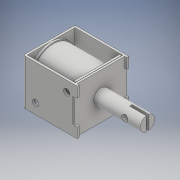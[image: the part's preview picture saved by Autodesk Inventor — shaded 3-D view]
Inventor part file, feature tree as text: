
AUTODESK INVENTOR PART (.ipt)
format: ipt  version: 2017 (Build 210142000, 142)  size: 295,936 bytes
history: native  units: mm
features: extrude x14, sketch x14, other x5, mirror x4, fillet x3
ambient origin geometry x8: Origin, YZ Plane, XZ Plane, XY Plane, X Axis, Y Axis, Z Axis, Center Point
bodies: Body1 (feature_tree)
feature tree (40):
  other  "Твердое тело1"
  extrude  "Выдавливание1"  Depth=25.0mm
  extrude  "Выдавливание4"  Depth=26.0mm
  extrude  "Выдавливание5"  Depth=22.0mm TaperAngle=0.0deg
  extrude  "Выдавливание6"  Depth=1.0mm
  extrude  "Выдавливание7"  Depth=1.0mm
  extrude  "Выдавливание8"  Depth=1.0mm
  other  "РабПлоскость1"
  extrude  "Выдавливание11"  Depth=25.0mm TaperAngle=0.0deg
  other  "РабПлоскость2"
  extrude  "Выдавливание12"  Depth=5.0mm
  extrude  "Выдавливание13"  Depth=5.0mm
  mirror  "Зеркальное отражение1"
  mirror  "Зеркальное отражение2"
  extrude  "Выдавливание14"  Depth=2.0mm
  other  "РабПлоскость3"
  extrude  "Выдавливание15"  Depth=25.0mm TaperAngle=0.0deg
  mirror  "Зеркальное отражение3"
  fillet  "Сопряжение1"  Radius=22.0mm
  fillet  "Сопряжение2"  Radius=1.0mm
  other  "РабПлоскость4"
  extrude  "Выдавливание16"  Depth=21.0mm
  mirror  "Зеркальное отражение4"
  extrude  "Выдавливание17"  Depth=21.0mm TaperAngle=0.0deg
  fillet  "Сопряжение5"  Radius=1.0mm
  extrude  "Выдавливание18"  Depth=1.0mm
  sketch  "Эскиз1"
  sketch  "Эскиз4"
  sketch  "Эскиз5"
  sketch  "Эскиз6"
  sketch  "Эскиз7"
  sketch  "Эскиз8"
  sketch  "Эскиз13"
  sketch  "Эскиз14"
  sketch  "Эскиз15"
  sketch  "Эскиз16"
  sketch  "Эскиз17"
  sketch  "Эскиз18"
  sketch  "Эскиз19"
  sketch  "Эскиз20"
